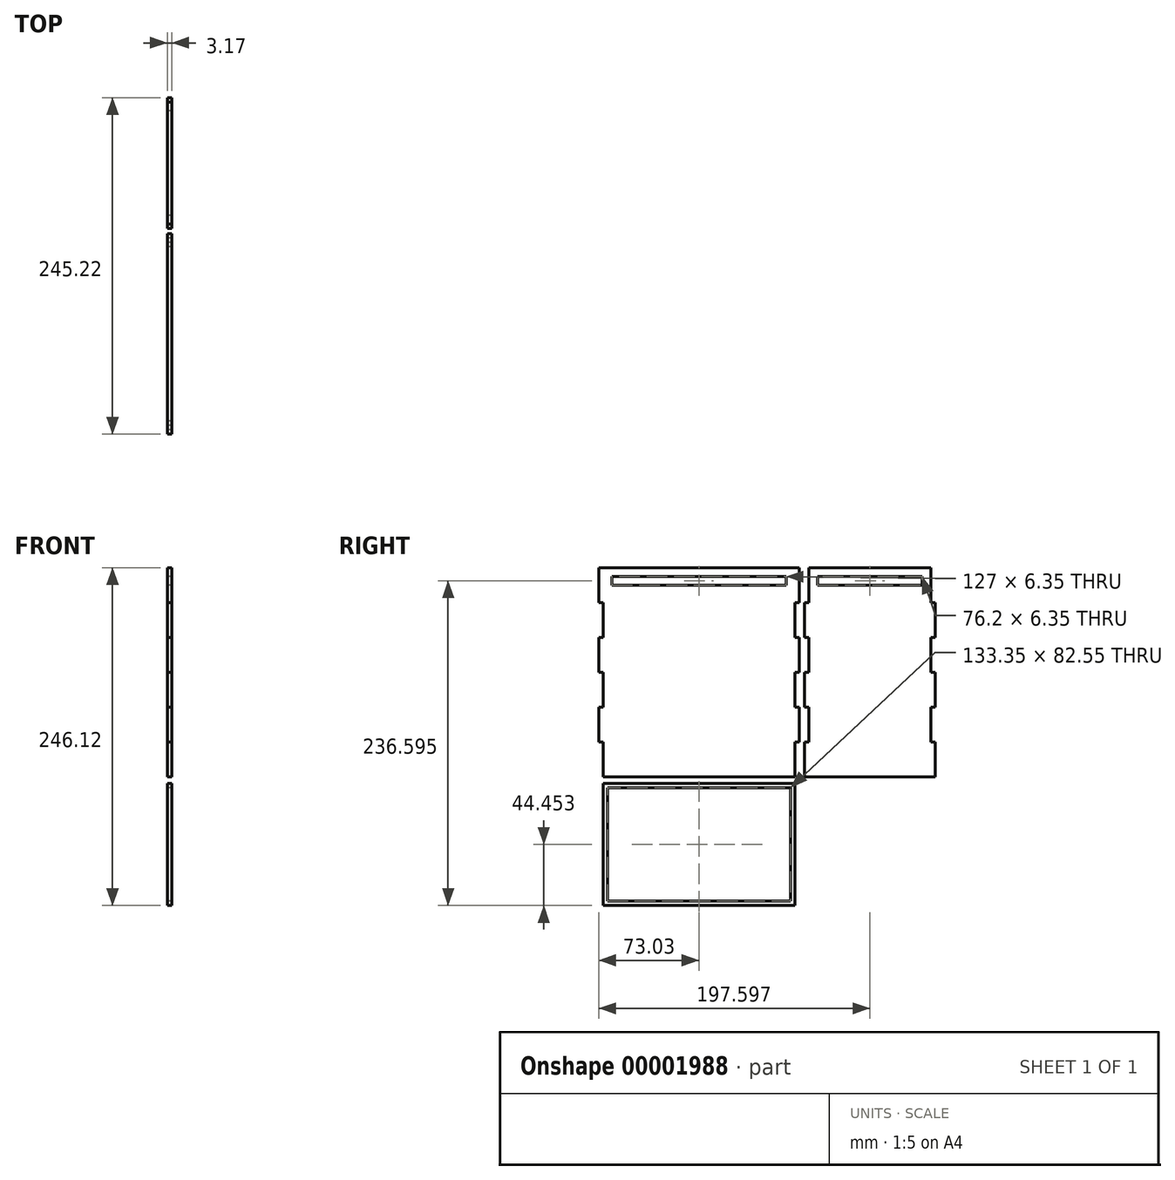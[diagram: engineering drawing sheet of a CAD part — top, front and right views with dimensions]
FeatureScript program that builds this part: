
annotation { "Feature Type Name" : "Feature", "Feature Type Description" : "" }
export const myFeature = defineFeature(function(context is Context, id is Id, definition is map)
    precondition{}
    {
        {
            var Q0;
            Q0=qCreatedBy(makeId("Right.planeOp"),FACE);
            var sketch = newSketch(context, id + "F0", { "sketchPlane" : qUnion([Q0])});
            skLineSegment(sketch, "E0.bottom", {"start": v(0, 0) * mm, "end": v(139.7, 0) * mm});
            skLineSegment(sketch, "E0.top", {"start": v(0, 152.4) * mm, "end": v(139.7, 152.4) * mm});
            skLineSegment(sketch, "E0.left", {"start": v(0, 0) * mm, "end": v(0, 25.4) * mm});
            skLineSegment(sketch, "E0.right", {"start": v(139.7, 0) * mm, "end": v(139.7, 25.4) * mm});
            skLineSegment(sketch, "E1", {"start": v(-3.18, 25.4) * mm, "end": v(-3.18, 50.8) * mm});
            skLineSegment(sketch, "E2", {"start": v(0, 152.4) * mm, "end": v(-3.18, 152.4) * mm});
            skLineSegment(sketch, "E3", {"start": v(0, 76.2) * mm, "end": v(-3.18, 76.2) * mm});
            skLineSegment(sketch, "E4", {"start": v(0, 50.8) * mm, "end": v(-3.18, 50.8) * mm});
            skLineSegment(sketch, "E5", {"start": v(0, 25.4) * mm, "end": v(-3.18, 25.4) * mm});
            skLineSegment(sketch, "E6", {"start": v(0, 101.6) * mm, "end": v(-3.18, 101.6) * mm});
            skLineSegment(sketch, "E7", {"start": v(0, 127) * mm, "end": v(-3.17, 127) * mm});
            skLineSegment(sketch, "E8.trimOffspring", {"start": v(-3.18, 127) * mm, "end": v(-3.18, 152.4) * mm});
            skLineSegment(sketch, "E9.trimOffspring", {"start": v(0, 101.6) * mm, "end": v(0, 127) * mm});
            skLineSegment(sketch, "E10.trimOffspring", {"start": v(-3.18, 76.2) * mm, "end": v(-3.18, 101.6) * mm});
            skLineSegment(sketch, "E11.trimOffspring", {"start": v(0, 50.8) * mm, "end": v(0, 76.2) * mm});
            skPoint(sketch, "E12.end.orphan", {"position": v(-3.17, 0) * mm});
            skLineSegment(sketch, "E13", {"start": v(69.85, 0) * mm, "end": v(69.85, 152.4) * mm, "construction": true});
            skLineSegment(sketch, "E14.0.MirrorCS", {"start": v(139.7, 101.6) * mm, "end": v(142.88, 101.6) * mm});
            skLineSegment(sketch, "E14.1.MirrorCS", {"start": v(139.7, 127) * mm, "end": v(142.87, 127) * mm});
            skLineSegment(sketch, "E14.2.MirrorCS", {"start": v(139.7, 76.2) * mm, "end": v(142.88, 76.2) * mm});
            skLineSegment(sketch, "E14.3.MirrorCS", {"start": v(139.7, 50.8) * mm, "end": v(142.88, 50.8) * mm});
            skLineSegment(sketch, "E14.4.MirrorCS", {"start": v(139.7, 25.4) * mm, "end": v(142.88, 25.4) * mm});
            skLineSegment(sketch, "E14.5.MirrorCS", {"start": v(139.7, 152.4) * mm, "end": v(142.87, 152.4) * mm});
            skLineSegment(sketch, "E14.6.MirrorCS", {"start": v(139.7, 50.8) * mm, "end": v(139.7, 76.2) * mm});
            skLineSegment(sketch, "E14.7.MirrorCS", {"start": v(139.7, 101.6) * mm, "end": v(139.7, 127) * mm});
            skLineSegment(sketch, "E14.8.MirrorCS", {"start": v(142.88, 127) * mm, "end": v(142.88, 152.4) * mm});
            skPoint(sketch, "E14.9.MirrorP", {"position": v(142.88, 0) * mm});
            skLineSegment(sketch, "E14.10.MirrorCS", {"start": v(142.88, 76.2) * mm, "end": v(142.88, 101.6) * mm});
            skLineSegment(sketch, "E14.11.MirrorCS", {"start": v(142.88, 25.4) * mm, "end": v(142.88, 50.8) * mm});
            skLineSegment(sketch, "E15.bottom", {"start": v(149.97, 0) * mm, "end": v(238.87, 0) * mm});
            skLineSegment(sketch, "E15.top", {"start": v(149.97, 152.4) * mm, "end": v(238.87, 152.4) * mm});
            skLineSegment(sketch, "E15.left", {"start": v(149.97, 25.4) * mm, "end": v(149.97, 50.8) * mm});
            skLineSegment(sketch, "E15.right", {"start": v(238.87, 25.4) * mm, "end": v(238.87, 50.8) * mm});
            skLineSegment(sketch, "E16", {"start": v(149.97, 127) * mm, "end": v(146.8, 127) * mm});
            skLineSegment(sketch, "E17", {"start": v(146.8, 127) * mm, "end": v(146.8, 101.6) * mm});
            skLineSegment(sketch, "E18", {"start": v(146.8, 101.6) * mm, "end": v(149.97, 101.6) * mm});
            skLineSegment(sketch, "E19", {"start": v(149.97, 76.2) * mm, "end": v(146.8, 76.2) * mm});
            skLineSegment(sketch, "E20", {"start": v(146.8, 76.2) * mm, "end": v(146.8, 50.8) * mm});
            skLineSegment(sketch, "E21", {"start": v(146.8, 50.8) * mm, "end": v(149.97, 50.8) * mm});
            skLineSegment(sketch, "E22", {"start": v(149.97, 25.4) * mm, "end": v(146.8, 25.4) * mm});
            skLineSegment(sketch, "E23", {"start": v(146.8, 25.4) * mm, "end": v(146.8, 0) * mm});
            skLineSegment(sketch, "E24", {"start": v(146.8, 0) * mm, "end": v(149.97, 0) * mm});
            skLineSegment(sketch, "E25.trimOffspring", {"start": v(149.97, 76.2) * mm, "end": v(149.97, 101.6) * mm});
            skLineSegment(sketch, "E26.trimOffspring", {"start": v(149.97, 127) * mm, "end": v(149.97, 152.4) * mm});
            skLineSegment(sketch, "E27", {"start": v(194.42, 152.4) * mm, "end": v(194.42, 0) * mm, "construction": true});
            skLineSegment(sketch, "E28.0.MirrorCS", {"start": v(242.04, 101.6) * mm, "end": v(238.87, 101.6) * mm});
            skLineSegment(sketch, "E28.1.MirrorCS", {"start": v(242.04, 50.8) * mm, "end": v(238.87, 50.8) * mm});
            skLineSegment(sketch, "E28.2.MirrorCS", {"start": v(238.87, 127) * mm, "end": v(242.04, 127) * mm});
            skLineSegment(sketch, "E28.3.MirrorCS", {"start": v(242.04, 0) * mm, "end": v(238.87, 0) * mm});
            skLineSegment(sketch, "E28.4.MirrorCS", {"start": v(238.87, 25.4) * mm, "end": v(242.04, 25.4) * mm});
            skLineSegment(sketch, "E28.5.MirrorCS", {"start": v(238.87, 76.2) * mm, "end": v(242.04, 76.2) * mm});
            skLineSegment(sketch, "E28.6.MirrorCS", {"start": v(238.87, 127) * mm, "end": v(238.87, 152.4) * mm});
            skLineSegment(sketch, "E28.7.MirrorCS", {"start": v(242.04, 127) * mm, "end": v(242.04, 101.6) * mm});
            skLineSegment(sketch, "E28.9.MirrorCS", {"start": v(242.04, 25.4) * mm, "end": v(242.04, 0) * mm});
            skLineSegment(sketch, "E28.10.MirrorCS", {"start": v(238.87, 76.2) * mm, "end": v(238.87, 101.6) * mm});
            skLineSegment(sketch, "E28.11.MirrorCS", {"start": v(242.04, 76.2) * mm, "end": v(242.04, 50.8) * mm});
            skLineSegment(sketch, "E29.bottom", {"start": v(0, -4.82) * mm, "end": v(139.7, -4.82) * mm});
            skLineSegment(sketch, "E29.top", {"start": v(0, -93.72) * mm, "end": v(139.7, -93.72) * mm});
            skLineSegment(sketch, "E29.left", {"start": v(0, -4.82) * mm, "end": v(0, -93.72) * mm});
            skLineSegment(sketch, "E29.right", {"start": v(139.7, -4.82) * mm, "end": v(139.7, -93.72) * mm});
            skLineSegment(sketch, "E30.0", {"start": v(3.17, -8) * mm, "end": v(136.53, -8) * mm});
            skLineSegment(sketch, "E30.1", {"start": v(3.17, -8) * mm, "end": v(3.18, -90.54) * mm});
            skLineSegment(sketch, "E30.2", {"start": v(3.17, -90.54) * mm, "end": v(136.53, -90.54) * mm});
            skLineSegment(sketch, "E30.3", {"start": v(136.52, -8) * mm, "end": v(136.52, -90.54) * mm});
            skLineSegment(sketch, "E31.bottom", {"start": v(6.35, 146.05) * mm, "end": v(133.35, 146.05) * mm});
            skLineSegment(sketch, "E31.top", {"start": v(6.35, 139.7) * mm, "end": v(133.35, 139.7) * mm});
            skLineSegment(sketch, "E31.left", {"start": v(6.35, 146.05) * mm, "end": v(6.35, 139.7) * mm});
            skLineSegment(sketch, "E31.right", {"start": v(133.35, 146.05) * mm, "end": v(133.35, 139.7) * mm});
            skLineSegment(sketch, "E32.bottom", {"start": v(156.32, 146.05) * mm, "end": v(232.52, 146.05) * mm});
            skLineSegment(sketch, "E32.top", {"start": v(156.32, 139.7) * mm, "end": v(232.52, 139.7) * mm});
            skLineSegment(sketch, "E32.left", {"start": v(156.32, 146.05) * mm, "end": v(156.32, 139.7) * mm});
            skLineSegment(sketch, "E32.right", {"start": v(232.52, 146.05) * mm, "end": v(232.52, 139.7) * mm});
            skSolve(sketch);
        }
        {
            var Q0;
            Q0=makeQuery(id+"F0.imprint","IMPRINT",FACE,{"disambiguationData":[TD([[makeQuery(id+"F0.imprint","IMPRINT",EDGE,{"derivedFrom":sQuery(id+"F0.wireOp",EDGE,"E0.bottom")}),1.0]])]});
            var Q1;
            Q1=makeQuery(id+"F0.imprint","IMPRINT",FACE,{"disambiguationData":[TD([[makeQuery(id+"F0.imprint","IMPRINT",EDGE,{"derivedFrom":sQuery(id+"F0.wireOp",EDGE,"E15.bottom")}),1.0]])]});
            var Q2;
            Q2=makeQuery(id+"F0.imprint","IMPRINT",FACE,{"disambiguationData":[TD([[makeQuery(id+"F0.imprint","IMPRINT",EDGE,{"derivedFrom":sQuery(id+"F0.wireOp",EDGE,"E29.bottom")}),-1.0]])]});
            extrude(context, id + "F1", {"entities" : qUnion([Q0, Q1, Q2]), "depth" : 3.17 * mm});
        }
    });
